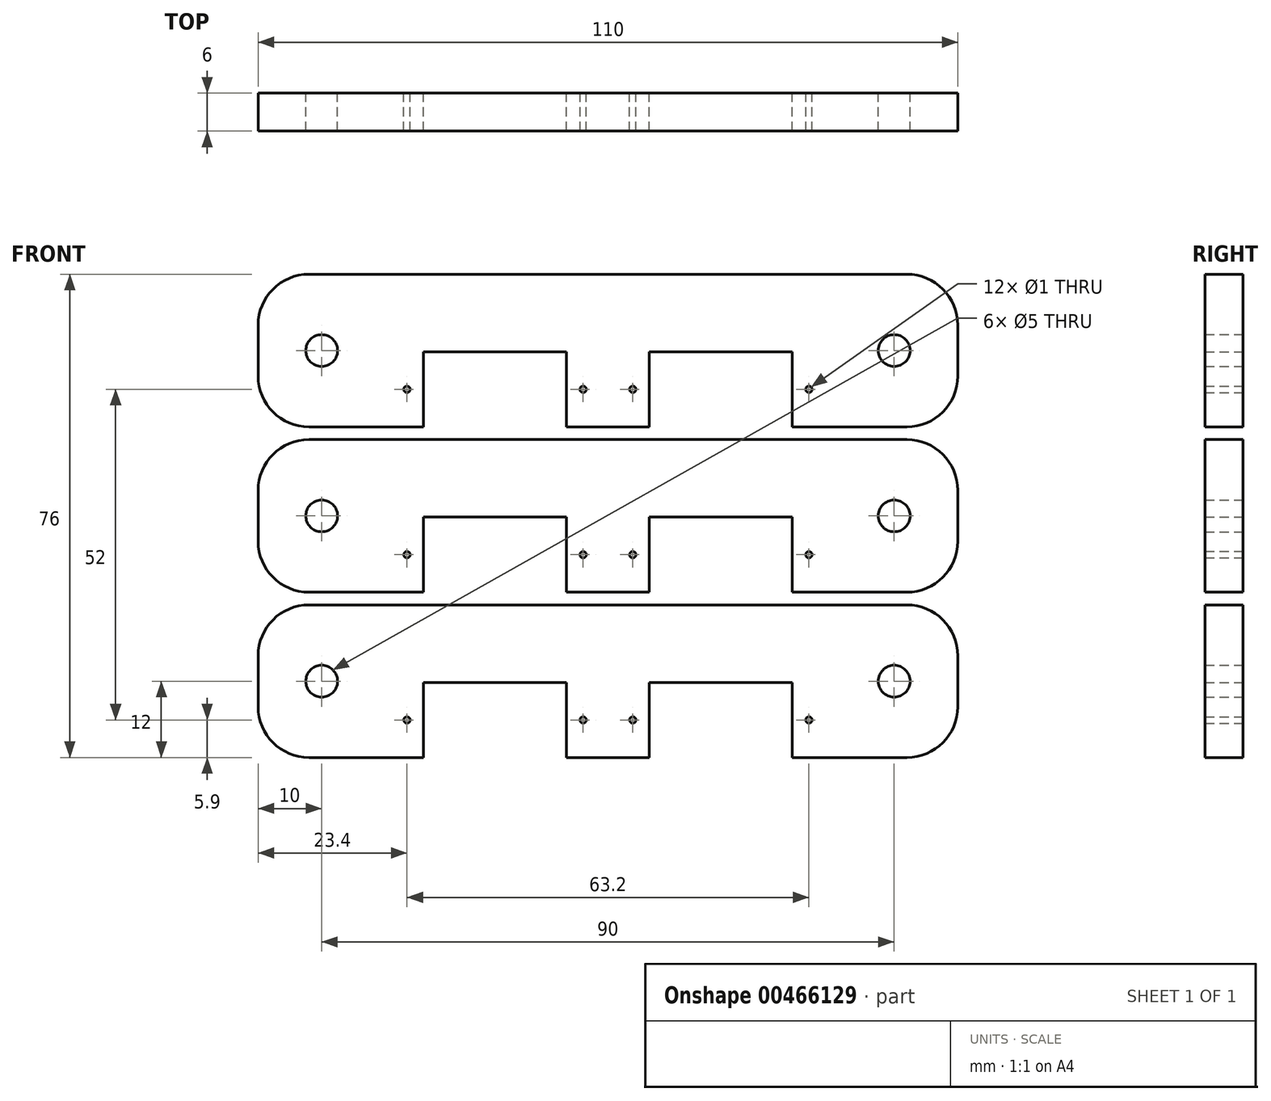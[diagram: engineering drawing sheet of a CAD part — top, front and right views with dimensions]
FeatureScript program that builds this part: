
annotation { "Feature Type Name" : "Feature", "Feature Type Description" : "" }
export const myFeature = defineFeature(function(context is Context, id is Id, definition is map)
    precondition{}
    {
        {
            var Q0;
            Q0=qCreatedBy(makeId("Front.planeOp"),FACE);
            var sketch = newSketch(context, id + "F0", { "sketchPlane" : qUnion([Q0])});
            skLineSegment(sketch, "E0.bottom", {"start": v(-47, 12) * mm, "end": v(47, 12) * mm});
            skLineSegment(sketch, "E0.left", {"start": v(-55, 4) * mm, "end": v(-55, -4) * mm});
            skLineSegment(sketch, "E0.right", {"start": v(55, 4) * mm, "end": v(55, -4) * mm});
            skLineSegment(sketch, "E1.bottom", {"start": v(-29, -12) * mm, "end": v(-29, -0.2) * mm});
            skLineSegment(sketch, "E1.top", {"start": v(-6.5, -12) * mm, "end": v(-6.5, -0.2) * mm});
            skLineSegment(sketch, "E1.right", {"start": v(-29, -0.2) * mm, "end": v(-6.5, -0.2) * mm});
            skCircle(sketch, "E2", {"center": v(-45, 0) * mm, "radius": 2.5 * mm});
            skCircle(sketch, "E3", {"center": v(45, 0) * mm, "radius": 2.5 * mm});
            skCircle(sketch, "E4", {"center": v(-3.9, -6.1) * mm, "radius": 0.5 * mm});
            skCircle(sketch, "E5", {"center": v(-31.6, -6.1) * mm, "radius": 0.5 * mm});
            skPoint(sketch, "E6.visualSharp", {"position": v(-55, 12) * mm});
            skArc(sketch, "E6.filletArc", {"start": v(-47, 12) * mm, "mid": v(-52.66, 9.66) * mm, "end": v(-55, 4) * mm});
            skPoint(sketch, "E7.visualSharp", {"position": v(55, 12) * mm});
            skArc(sketch, "E7.filletArc", {"start": v(55, 4) * mm, "mid": v(52.66, 9.66) * mm, "end": v(47, 12) * mm});
            skPoint(sketch, "E8.visualSharp", {"position": v(55, -12) * mm});
            skArc(sketch, "E8.filletArc", {"start": v(47, -12) * mm, "mid": v(52.66, -9.66) * mm, "end": v(55, -4) * mm});
            skPoint(sketch, "E9.visualSharp", {"position": v(-55, -12) * mm});
            skArc(sketch, "E9.filletArc", {"start": v(-55, -4) * mm, "mid": v(-52.66, -9.66) * mm, "end": v(-47, -12) * mm});
            skLineSegment(sketch, "E10", {"start": v(-35, 12) * mm, "end": v(-35, -12) * mm, "construction": true});
            skLineSegment(sketch, "E11", {"start": v(35, -12) * mm, "end": v(35, 12) * mm, "construction": true});
            skCircle(sketch, "E12.MirrorC", {"center": v(31.6, -6.1) * mm, "radius": 0.5 * mm});
            skCircle(sketch, "E13.MirrorC", {"center": v(3.9, -6.1) * mm, "radius": 0.5 * mm});
            skLineSegment(sketch, "E14.MirrorCS", {"start": v(29, -12) * mm, "end": v(29, -0.2) * mm});
            skLineSegment(sketch, "E15.MirrorCS", {"start": v(29, -0.2) * mm, "end": v(6.5, -0.2) * mm});
            skLineSegment(sketch, "E16.MirrorCS", {"start": v(6.5, -12) * mm, "end": v(6.5, -0.2) * mm});
            skLineSegment(sketch, "E17", {"start": v(-47, -12) * mm, "end": v(-29, -12) * mm});
            skLineSegment(sketch, "E18", {"start": v(-6.5, -12) * mm, "end": v(6.5, -12) * mm});
            skLineSegment(sketch, "E19", {"start": v(29, -12) * mm, "end": v(47, -12) * mm});
            skLineSegment(sketch, "E20", {"start": v(-31.6, -6.1) * mm, "end": v(31.6, -6.1) * mm, "construction": true});
            skLineSegment(sketch, "E21.0.1.0", {"start": v(-29, 14) * mm, "end": v(-29, 25.8) * mm});
            skLineSegment(sketch, "E21.0.1.1", {"start": v(55, 30) * mm, "end": v(55, 22) * mm});
            skLineSegment(sketch, "E21.0.1.2", {"start": v(-55, 30) * mm, "end": v(-55, 22) * mm});
            skLineSegment(sketch, "E21.0.1.3", {"start": v(-47, 38) * mm, "end": v(47, 38) * mm});
            skArc(sketch, "E21.0.1.4", {"start": v(-55, 22) * mm, "mid": v(-52.66, 16.34) * mm, "end": v(-47, 14) * mm});
            skLineSegment(sketch, "E21.0.1.5", {"start": v(-6.5, 14) * mm, "end": v(6.5, 14) * mm});
            skPoint(sketch, "E21.0.1.6", {"position": v(55, 38) * mm});
            skLineSegment(sketch, "E21.0.1.7", {"start": v(-29, 25.8) * mm, "end": v(-6.5, 25.8) * mm});
            skCircle(sketch, "E21.0.1.8", {"center": v(-45, 26) * mm, "radius": 2.5 * mm});
            skLineSegment(sketch, "E21.0.1.9", {"start": v(-47, 14) * mm, "end": v(-29, 14) * mm});
            skLineSegment(sketch, "E21.0.1.10", {"start": v(-35, 38) * mm, "end": v(-35, 14) * mm, "construction": true});
            skCircle(sketch, "E21.0.1.11", {"center": v(45, 26) * mm, "radius": 2.5 * mm});
            skLineSegment(sketch, "E21.0.1.12", {"start": v(-6.5, 14) * mm, "end": v(-6.5, 25.8) * mm});
            skPoint(sketch, "E21.0.1.13", {"position": v(-55, 14) * mm});
            skLineSegment(sketch, "E21.0.1.14", {"start": v(35, 14) * mm, "end": v(35, 38) * mm, "construction": true});
            skLineSegment(sketch, "E21.0.1.15", {"start": v(29, 14) * mm, "end": v(29, 25.8) * mm});
            skLineSegment(sketch, "E21.0.1.16", {"start": v(29, 14) * mm, "end": v(47, 14) * mm});
            skArc(sketch, "E21.0.1.17", {"start": v(47, 14) * mm, "mid": v(52.66, 16.34) * mm, "end": v(55, 22) * mm});
            skPoint(sketch, "E21.0.1.18", {"position": v(55, 14) * mm});
            skPoint(sketch, "E21.0.1.19", {"position": v(-55, 38) * mm});
            skLineSegment(sketch, "E21.0.1.20", {"start": v(29, 25.8) * mm, "end": v(6.5, 25.8) * mm});
            skLineSegment(sketch, "E21.0.1.21", {"start": v(6.5, 14) * mm, "end": v(6.5, 25.8) * mm});
            skLineSegment(sketch, "E21.0.1.22", {"start": v(-31.6, 19.9) * mm, "end": v(31.6, 19.9) * mm, "construction": true});
            skArc(sketch, "E21.0.1.23", {"start": v(-47, 38) * mm, "mid": v(-52.66, 35.66) * mm, "end": v(-55, 30) * mm});
            skArc(sketch, "E21.0.1.24", {"start": v(55, 30) * mm, "mid": v(52.66, 35.66) * mm, "end": v(47, 38) * mm});
            skCircle(sketch, "E21.0.1.25", {"center": v(-3.9, 19.9) * mm, "radius": 0.5 * mm});
            skCircle(sketch, "E21.0.1.26", {"center": v(3.9, 19.9) * mm, "radius": 0.5 * mm});
            skCircle(sketch, "E21.0.1.27", {"center": v(31.6, 19.9) * mm, "radius": 0.5 * mm});
            skCircle(sketch, "E21.0.1.28", {"center": v(-31.6, 19.9) * mm, "radius": 0.5 * mm});
            skLineSegment(sketch, "E21.0.2.0", {"start": v(-29, 40) * mm, "end": v(-29, 51.8) * mm});
            skLineSegment(sketch, "E21.0.2.1", {"start": v(55, 56) * mm, "end": v(55, 48) * mm});
            skLineSegment(sketch, "E21.0.2.2", {"start": v(-55, 56) * mm, "end": v(-55, 48) * mm});
            skLineSegment(sketch, "E21.0.2.3", {"start": v(-47, 64) * mm, "end": v(47, 64) * mm});
            skArc(sketch, "E21.0.2.4", {"start": v(-55, 48) * mm, "mid": v(-52.66, 42.34) * mm, "end": v(-47, 40) * mm});
            skLineSegment(sketch, "E21.0.2.5", {"start": v(-6.5, 40) * mm, "end": v(6.5, 40) * mm});
            skPoint(sketch, "E21.0.2.6", {"position": v(55, 64) * mm});
            skLineSegment(sketch, "E21.0.2.7", {"start": v(-29, 51.8) * mm, "end": v(-6.5, 51.8) * mm});
            skCircle(sketch, "E21.0.2.8", {"center": v(-45, 52) * mm, "radius": 2.5 * mm});
            skLineSegment(sketch, "E21.0.2.9", {"start": v(-47, 40) * mm, "end": v(-29, 40) * mm});
            skLineSegment(sketch, "E21.0.2.10", {"start": v(-35, 64) * mm, "end": v(-35, 40) * mm, "construction": true});
            skCircle(sketch, "E21.0.2.11", {"center": v(45, 52) * mm, "radius": 2.5 * mm});
            skLineSegment(sketch, "E21.0.2.12", {"start": v(-6.5, 40) * mm, "end": v(-6.5, 51.8) * mm});
            skPoint(sketch, "E21.0.2.13", {"position": v(-55, 40) * mm});
            skLineSegment(sketch, "E21.0.2.14", {"start": v(35, 40) * mm, "end": v(35, 64) * mm, "construction": true});
            skLineSegment(sketch, "E21.0.2.15", {"start": v(29, 40) * mm, "end": v(29, 51.8) * mm});
            skLineSegment(sketch, "E21.0.2.16", {"start": v(29, 40) * mm, "end": v(47, 40) * mm});
            skArc(sketch, "E21.0.2.17", {"start": v(47, 40) * mm, "mid": v(52.66, 42.34) * mm, "end": v(55, 48) * mm});
            skPoint(sketch, "E21.0.2.18", {"position": v(55, 40) * mm});
            skPoint(sketch, "E21.0.2.19", {"position": v(-55, 64) * mm});
            skLineSegment(sketch, "E21.0.2.20", {"start": v(29, 51.8) * mm, "end": v(6.5, 51.8) * mm});
            skLineSegment(sketch, "E21.0.2.21", {"start": v(6.5, 40) * mm, "end": v(6.5, 51.8) * mm});
            skLineSegment(sketch, "E21.0.2.22", {"start": v(-31.6, 45.9) * mm, "end": v(31.6, 45.9) * mm, "construction": true});
            skArc(sketch, "E21.0.2.23", {"start": v(-47, 64) * mm, "mid": v(-52.66, 61.66) * mm, "end": v(-55, 56) * mm});
            skArc(sketch, "E21.0.2.24", {"start": v(55, 56) * mm, "mid": v(52.66, 61.66) * mm, "end": v(47, 64) * mm});
            skCircle(sketch, "E21.0.2.25", {"center": v(-3.9, 45.9) * mm, "radius": 0.5 * mm});
            skCircle(sketch, "E21.0.2.26", {"center": v(3.9, 45.9) * mm, "radius": 0.5 * mm});
            skCircle(sketch, "E21.0.2.27", {"center": v(31.6, 45.9) * mm, "radius": 0.5 * mm});
            skCircle(sketch, "E21.0.2.28", {"center": v(-31.6, 45.9) * mm, "radius": 0.5 * mm});
            skLineSegment(sketch, "E21.direction1", {"start": v(-55, -12) * mm, "end": v(65, -12) * mm, "construction": true});
            skLineSegment(sketch, "E21.direction2", {"start": v(-55, -12) * mm, "end": v(-55, 14) * mm, "construction": true});
            skSolve(sketch);
        }
        {
            var Q0;
            Q0 = qSketchRegion(id + "F0", true);
            extrude(context, id + "F1", {"entities" : qUnion([Q0]), "depth" : 6 * mm});
        }
    });
